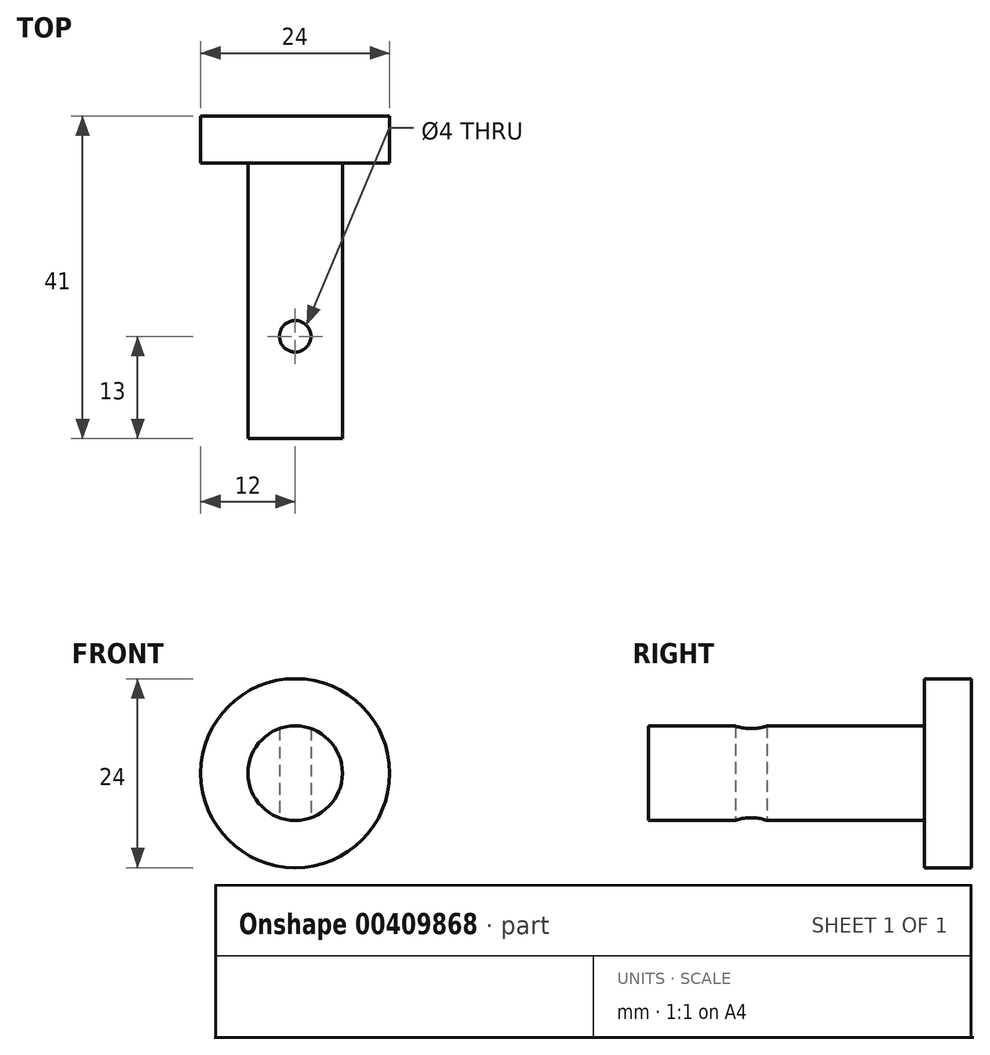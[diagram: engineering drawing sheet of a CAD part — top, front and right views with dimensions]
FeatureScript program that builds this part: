
annotation { "Feature Type Name" : "Feature", "Feature Type Description" : "" }
export const myFeature = defineFeature(function(context is Context, id is Id, definition is map)
    precondition{}
    {
        {
            var Q0;
            Q0=qCreatedBy(makeId("Top.planeOp"),FACE);
            var sketch = newSketch(context, id + "F0", { "sketchPlane" : qUnion([Q0])});
            skLineSegment(sketch, "E0", {"start": v(0, 41) * mm, "end": v(-12, 41) * mm});
            skLineSegment(sketch, "E1", {"start": v(-12, 41) * mm, "end": v(-12, 35) * mm});
            skLineSegment(sketch, "E2", {"start": v(-12, 35) * mm, "end": v(-6, 35) * mm});
            skLineSegment(sketch, "E3", {"start": v(-6, 35) * mm, "end": v(-6, 0) * mm});
            skLineSegment(sketch, "E4", {"start": v(-6, 0) * mm, "end": v(0, 0) * mm});
            skLineSegment(sketch, "E5", {"start": v(0, 41) * mm, "end": v(0, 0) * mm});
            skSolve(sketch);
        }
        {
            var Q0;
            Q0=qSketchRegion(id+"F0",true);
            var Q1;
            Q1=sQuery(id+"F0.wireOp",EDGE,"E5");
            revolve(context, id + "F1", {"entities" : qUnion([Q0]), "axis" : qUnion([Q1]), "revolveType" : RevolveType.FULL});
        }
        {
            var Q0;
            Q0=qCreatedBy(makeId("Top.planeOp"),FACE);
            var sketch = newSketch(context, id + "F2", { "sketchPlane" : qUnion([Q0])});
            skCircle(sketch, "E6", {"center": v(0, 13) * mm, "radius": 2 * mm});
            skSolve(sketch);
        }
        {
            var Q0;
            Q0=qSketchRegion(id+"F2",true);
            extrude(context, id + "F3", {"entities" : qUnion([Q0]), "operationType" : NewBodyOperationType.REMOVE, "endBound" : BoundingType.SYMMETRIC, "depth" : 25 * mm});
        }
    });
